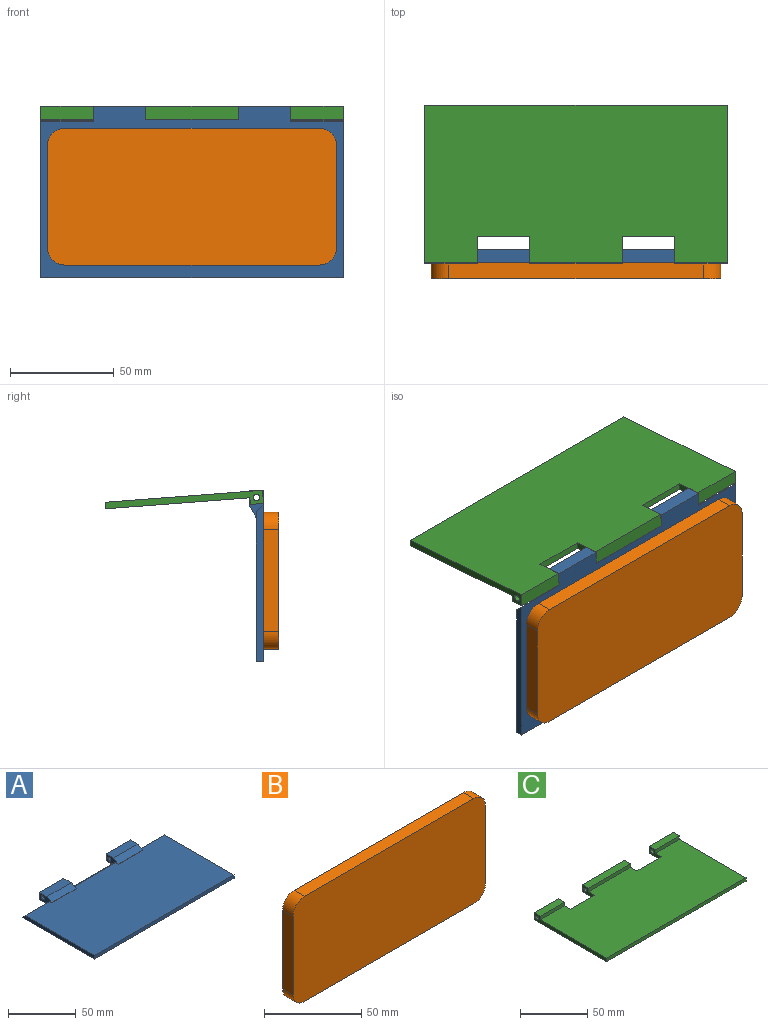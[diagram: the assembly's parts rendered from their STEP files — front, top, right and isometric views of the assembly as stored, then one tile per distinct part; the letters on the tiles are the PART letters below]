
ASSEMBLY  parts=3 mates=2
PART A: 23 faces, bbox 146.1x82.6x6.4 mm
  f0: plane 44.45x0.64mm, normal (0,1,0), area 28.2mm2, adj f5,f7,f9,f20
  f1: plane 75.57x3.18mm, normal (-1,0,0), area 234.9mm2, adj f2,f4,f5,f21
  f2: plane 146.05x3.18mm, normal (0,-1,0), area 463.7mm2, adj f1,f3,f4,f5
  f3: plane 75.57x3.18mm, normal (1,0,0), area 234.9mm2, adj f2,f4,f5,f22
  f4: plane 146.05x73.03mm, normal (0,0,1), area 10471.8mm2, adj f1,f2,f3,f6,f7,f9,f10,f16
  f5: plane 146.05x82.55mm, normal (0,0,-1), area 11419.3mm2, adj f0,f1,f2,f3,f6,f7,f8,f9
  f6: plane 12.7x6.35mm, normal (1,0,0), area 52.2mm2, adj f4,f5,f8,f13,f15,f17,f18,f22
  f7: plane 12.7x6.35mm, normal (-1,0,0), area 49.1mm2, adj f0,f4,f5,f8,f13,f15,f17,f18
  f8: plane 25.4x6.35mm, normal (0,1,0), area 161.3mm2, adj f5,f6,f7,f13
  f9: plane 12.7x6.35mm, normal (1,0,0), area 49.1mm2, adj f0,f4,f5,f11,f12,f14,f16,f19
  f10: plane 12.7x6.35mm, normal (-1,0,0), area 52.2mm2, adj f4,f5,f11,f12,f14,f16,f19,f21
  f11: plane 25.4x6.35mm, normal (0,1,0), area 161.3mm2, adj f5,f9,f10,f12
  f12: plane 25.4x7.62mm, normal (0,0,1), area 193.5mm2, adj f9,f10,f11,f19
  f13: plane 25.4x7.62mm, normal (0,0,1), area 193.5mm2, adj f6,f7,f8,f18
  f14: cylinder r=1.59mm len=25.4mm, axis (1,0,0), area 253.4mm2, adj f9,f10
  f15: cylinder r=1.59mm len=25.4mm, axis (1,0,0), area 253.4mm2, adj f6,f7
  f16: plane 25.4x0.24mm, normal (0,-1,0), area 6.1mm2, adj f4,f9,f10,f19
  f17: plane 25.4x0.24mm, normal (0,-1,0), area 6.1mm2, adj f4,f6,f7,f18
  f18: plane 25.4x5.08mm, normal (0,-0.5,0.87), area 149mm2, adj f6,f7,f13,f17
  f19: plane 25.4x5.08mm, normal (0,-0.5,0.87), area 149mm2, adj f9,f10,f12,f16
  f20: plane 44.45x3.18mm, normal (0,0.62,0.78), area 180.7mm2, adj f0,f4,f7,f9
  f21: plane 25.4x3.18mm, normal (0,0.71,0.71), area 114mm2, adj f1,f4,f5,f10
  f22: plane 25.4x3.18mm, normal (0,0.71,0.71), area 114mm2, adj f3,f4,f5,f6
PART B: 10 faces, bbox 139.7x7.6x66 mm
  f0: plane 122.94x7.62mm, normal (0,0,1), area 936.8mm2, adj f4,f5,f6,f9
  f1: plane 49.28x7.62mm, normal (-1,0,0), area 375.5mm2, adj f4,f5,f6,f7
  f2: plane 122.94x7.62mm, normal (0,0,-1), area 936.8mm2, adj f4,f5,f7,f8
  f3: plane 49.28x7.62mm, normal (1,0,0), area 375.5mm2, adj f4,f5,f8,f9
  f4: plane 139.7x66.04mm, normal (0,-1,0), area 9165.5mm2, adj f0,f1,f2,f3,f6,f7,f8,f9
  f5: plane 139.7x66.04mm, normal (0,1,0), area 9165.5mm2, adj f0,f1,f2,f3,f6,f7,f8,f9
  f6: cylinder r=8.38mm len=8.38mm, axis (0,-1,0), area 100.3mm2, adj f0,f1,f4,f5
  f7: cylinder r=8.38mm len=8.38mm, axis (0,1,0), area 100.3mm2, adj f1,f2,f4,f5
  f8: cylinder r=8.38mm len=8.38mm, axis (0,-1,0), area 100.3mm2, adj f2,f3,f4,f5
  f9: cylinder r=8.38mm len=8.38mm, axis (0,1,0), area 100.3mm2, adj f0,f3,f4,f5
PART C: 23 faces, bbox 146.1x76.2x6.4 mm
  f0: plane 146.05x69.85mm, normal (0,0,1), area 9879mm2, adj f4,f5,f6,f8,f9,f10,f11,f12
  f1: plane 44.45x6.35mm, normal (0,1,0), area 282.3mm2, adj f7,f8,f11,f13
  f2: plane 25.4x6.35mm, normal (0,1,0), area 161.3mm2, adj f6,f7,f9,f18
  f3: plane 25.4x6.35mm, normal (0,1,0), area 161.3mm2, adj f4,f7,f10,f16
  f4: plane 76.2x6.35mm, normal (-1,0,0), area 254.2mm2, adj f0,f3,f5,f7,f15,f16,f19
  f5: plane 146.05x3.18mm, normal (0,-1,0), area 463.7mm2, adj f0,f4,f6,f7
  f6: plane 76.2x6.35mm, normal (1,0,0), area 254.2mm2, adj f0,f2,f5,f7,f17,f18,f20
  f7: plane 146.05x76.2mm, normal (0,0,-1), area 10483.8mm2, adj f1,f2,f3,f4,f5,f6,f8,f9
  f8: plane 12.7x6.35mm, normal (1,0,0), area 52.6mm2, adj f0,f1,f7,f12,f13,f14,f21
  f9: plane 12.7x6.35mm, normal (-1,0,0), area 52.6mm2, adj f0,f2,f7,f17,f18,f20,f21
  f10: plane 12.7x6.35mm, normal (1,0,0), area 52.6mm2, adj f0,f3,f7,f15,f16,f19,f22
  f11: plane 12.7x6.35mm, normal (-1,0,0), area 52.6mm2, adj f0,f1,f7,f12,f13,f14,f22
  f12: plane 44.45x3.18mm, normal (0,-1,0), area 141.1mm2, adj f0,f8,f11,f13
  f13: plane 44.45x6.35mm, normal (0,0,1), area 282.3mm2, adj f1,f8,f11,f12
  f14: cylinder r=1.59mm len=44.45mm, axis (-1,0,0), area 443.4mm2, adj f8,f11
  f15: plane 25.4x3.18mm, normal (0,-1,0), area 80.6mm2, adj f0,f4,f10,f16
  f16: plane 25.4x6.35mm, normal (0,0,1), area 161.3mm2, adj f3,f4,f10,f15
  f17: plane 25.4x3.18mm, normal (0,-1,0), area 80.6mm2, adj f0,f6,f9,f18
  f18: plane 25.4x6.35mm, normal (0,0,1), area 161.3mm2, adj f2,f6,f9,f17
  f19: cylinder r=1.59mm len=25.4mm, axis (-1,0,0), area 253.4mm2, adj f4,f10
  f20: cylinder r=1.59mm len=25.4mm, axis (-1,0,0), area 253.4mm2, adj f6,f9
  f21: plane 25.4x3.18mm, normal (0,1,0), area 80.6mm2, adj f0,f7,f8,f9
  f22: plane 25.4x3.18mm, normal (0,1,0), area 80.6mm2, adj f0,f7,f10,f11
PLACE A rot(axis=(0,0.71,0.71),180deg) t=(0,0,-1.06)mm
PLACE B at identity
PLACE C rot(axis=(1,0,0),175.6deg) t=(0,38.24,40.73)mm
MATE fastened A.f5 <-> B.f5  axis (0,-1,0) through (0,0,0)mm
MATE revolute C.f14 <-> A.f14  axis (-1,0,0) through (-22.22,3.18,40.22)mm
